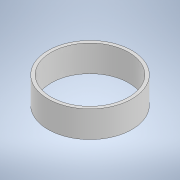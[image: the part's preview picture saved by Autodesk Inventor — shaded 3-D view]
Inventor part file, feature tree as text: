
AUTODESK INVENTOR PART (.ipt)
format: ipt  version: 2020 (Build 240168000, 168)  size: 98,816 bytes
history: native  units: in
note: dims shown in document units (in); Inventor stores cm internally (conversion verified against a paired STEP export)
features: extrude x1, sketch x1
ambient origin geometry x8: Origin, YZ Plane, XZ Plane, XY Plane, X Axis, Y Axis, Z Axis, Center Point
bodies: Solid1 (feature_tree)
feature tree (2):
  extrude  "Extrusion1"  Depth=1.0433in
  sketch  "Sketch1"  dims[d0=3.0512in d1=3.3012in d2=1.0433in d3=0.0in]
